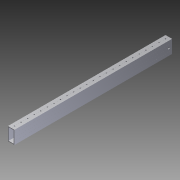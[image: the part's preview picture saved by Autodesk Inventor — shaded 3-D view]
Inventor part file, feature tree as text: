
AUTODESK INVENTOR PART (.ipt)
format: ipt  version: 2014 SP1 (Build 180222100, 222)  size: 741,376 bytes
history: native  units: in
note: dims shown in document units (in); Inventor stores cm internally (conversion verified against a paired STEP export)
features: other x2, extrude x2, sketch x2, imported_body x1
ambient origin geometry x8: Origin, YZ Plane, XZ Plane, XY Plane, X Axis, Y Axis, Z Axis, Center Point
bodies: Body1 (feature_tree)
feature tree (7):
  other  "Cut-Extrude2"
  other  "2x1 Tube1"
  extrude  "Extrusion1"  Depth=0.25in
  extrude  "Extrusion2"  Depth=1.0in TaperAngle=0.0deg
  imported_body  "Base1"
  sketch  "Sketch1"  dims[d0=35.0in d1=0.0in d2=0.25in]
  sketch  "Sketch2"  dims[d3=0.5in d4=1.0in d5=0.0in]
